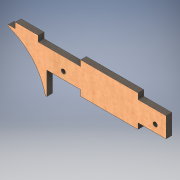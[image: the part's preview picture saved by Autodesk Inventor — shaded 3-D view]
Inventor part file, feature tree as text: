
AUTODESK INVENTOR PART (.ipt)
format: ipt  version: 2019 (Build 230136000, 136)  size: 154,112 bytes
history: native  units: mm
features: extrude x2, sketch x2, other x1
ambient origin geometry x8: Origin, YZ Plane, XZ Plane, XY Plane, X Axis, Y Axis, Z Axis, Center Point
bodies: Body1 (feature_tree)
feature tree (5):
  other  "Твердое тело1"
  extrude  "Выдавливание1"  Depth=14.0mm
  extrude  "Выдавливание2"  Depth=4.0mm
  sketch  "Эскиз1"
  sketch  "Эскиз2"
